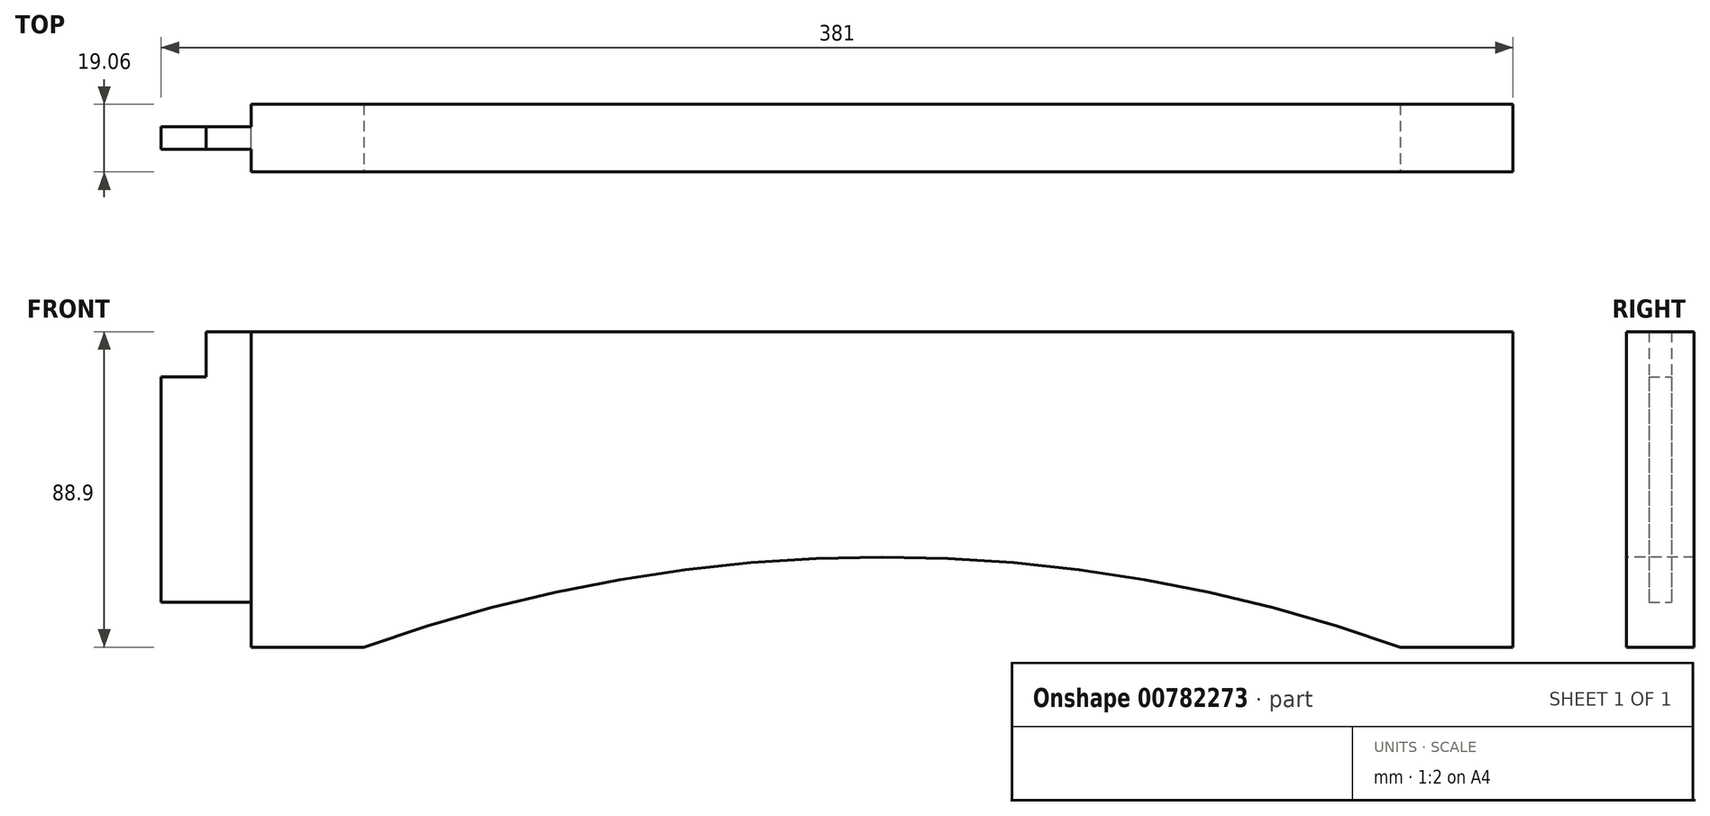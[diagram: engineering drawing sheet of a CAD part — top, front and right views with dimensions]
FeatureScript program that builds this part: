
annotation { "Feature Type Name" : "Feature", "Feature Type Description" : "" }
export const myFeature = defineFeature(function(context is Context, id is Id, definition is map)
    precondition{}
    {
        {
            var Q0;
            Q0=qCreatedBy(makeId("Front.planeOp"),FACE);
            var sketch = newSketch(context, id + "F0", { "sketchPlane" : qUnion([Q0])});
            skLineSegment(sketch, "E0.bottom", {"start": v(-177.8, 44.45) * mm, "end": v(177.8, 44.45) * mm});
            skLineSegment(sketch, "E0.top", {"start": v(-177.8, -44.45) * mm, "end": v(177.8, -44.45) * mm});
            skLineSegment(sketch, "E0.left", {"start": v(-177.8, 44.45) * mm, "end": v(-177.8, -44.45) * mm});
            skLineSegment(sketch, "E0.right", {"start": v(177.8, 44.45) * mm, "end": v(177.8, -44.45) * mm});
            skLineSegment(sketch, "E1", {"start": v(-177.8, 44.45) * mm, "end": v(177.8, -44.45) * mm, "construction": true});
            skSolve(sketch);
        }
        {
            var Q0;
            Q0 = qSketchRegion(id + "F0", true);
            extrude(context, id + "F1", {"entities" : qUnion([Q0]), "endBound" : BoundingType.SYMMETRIC, "depth" : 19.05 * mm, "offsetDistance" : 25.4 * mm});
        }
        {
            var Q0;
            Q0=qCreatedBy(makeId("Front.planeOp"),FACE);
            var sketch = newSketch(context, id + "F2", { "sketchPlane" : qUnion([Q0])});
            skLineSegment(sketch, "E2", {"start": v(-177.8, 44.45) * mm, "end": v(-190.5, 44.45) * mm});
            skLineSegment(sketch, "E3", {"start": v(-190.5, 44.45) * mm, "end": v(-190.5, 31.75) * mm});
            skLineSegment(sketch, "E4", {"start": v(-190.5, 31.75) * mm, "end": v(-203.2, 31.75) * mm});
            skLineSegment(sketch, "E5", {"start": v(-203.2, 31.75) * mm, "end": v(-203.2, -31.75) * mm});
            skLineSegment(sketch, "E6", {"start": v(-203.2, -31.75) * mm, "end": v(-177.8, -31.75) * mm});
            skPoint(sketch, "E7.0.end.orphan", {"position": v(-177.8, -44.45) * mm});
            skPoint(sketch, "E7.0.start.orphan", {"position": v(-177.8, 44.45) * mm});
            skLineSegment(sketch, "E8.0", {"start": v(-177.8, 44.45) * mm, "end": v(-177.8, -31.75) * mm});
            skSolve(sketch);
        }
        {
            var Q0;
            Q0 = qSketchRegion(id + "F2", true);
            extrude(context, id + "F3", {"entities" : qUnion([Q0]), "operationType" : NewBodyOperationType.ADD, "endBound" : BoundingType.SYMMETRIC, "depth" : 6.35 * mm, "offsetDistance" : 25.4 * mm});
        }
        {
            var Q0;
            Q0=makeQuery(id+"F1.opExtrude","CAP_FACE",FACE,{"disambiguationData":[OSD([sQuery(id+"F0.wireOp",EDGE,"E0.bottom"),sQuery(id+"F0.wireOp",EDGE,"E0.top"),sQuery(id+"F0.wireOp",EDGE,"E0.left"),sQuery(id+"F0.wireOp",EDGE,"E0.right")])],"isStart":false});
            var sketch = newSketch(context, id + "F4", { "sketchPlane" : qUnion([Q0])});
            skLineSegment(sketch, "E9", {"start": v(-146.05, -44.45) * mm, "end": v(146.05, -44.45) * mm});
            skArc(sketch, "E10", {"start": v(146.05, -44.45) * mm, "mid": v(0, -19.05) * mm, "end": v(-146.05, -44.45) * mm});
            skSolve(sketch);
        }
        {
            var Q0;
            Q0 = qSketchRegion(id + "F4", true);
            var Q1;
            Q1=makeQuery(id+"F1.opExtrude","CAP_FACE",FACE,{"disambiguationData":[OSD([sQuery(id+"F0.wireOp",EDGE,"E0.bottom"),sQuery(id+"F0.wireOp",EDGE,"E0.top"),sQuery(id+"F0.wireOp",EDGE,"E0.left"),sQuery(id+"F0.wireOp",EDGE,"E0.right")])],"isStart":true});
            extrude(context, id + "F5", {"entities" : qUnion([Q0]), "operationType" : NewBodyOperationType.REMOVE, "endBound" : BoundingType.UP_TO_SURFACE, "oppositeDirection" : true, "depth" : 25.4 * mm, "endBoundEntityFace" : qUnion([Q1]), "offsetDistance" : 25.4 * mm});
        }
    });
